# Revit family: super-g_super-g___l_1150mm_hl_dir_indirekt_led__27_6w_4260lm_3000k_cri_80_dali__430-1542_0726
name_source: partatom
category: Leuchten
revit_build: Autodesk Revit 2016 (Build: 20190508_0715(x64)
units: mm (PartAtom-declared; Revit-internal decimal feet)

## family parameters
Basisbauteil = Fläche
Beim Laden mit Abzugskörper schneiden = Nein
Bemaßung runder Anschluss = Durchmesser verwenden
Gemeinsam genutzt = Nein
Lichtquelle = Nein
Raumberechnungspunkt = Nein
Teiletyp = Normal

## types (1)
- 430-1542- (6 x LED, 710 lm, 5.1 W, 3000K)
    Approval mark = CE
    Beschreibung = The insert consists of aluminum-extruded profile. Charming SOFT-EDGE design ensure unparalleled styling. The ballast is integrated and allows for an operation with 220-240V (50/60Hz). SUPER-G (# 430-1542) is dimmable via BUS.
    CIE Flux Codes = 48 80 96 61 70
    Color Rendering = 1B/80…89
    Color Temperature = 3000K
    Height = 120 mm
    Hersteller = Prolicht
    Lamp Light Flux = 710 lm
    Lamp Power = 5.1 W
    Lamp count = 6
    Lampe = 6 x LED
    Length = 1150 mm
    Luminous efficacy = 97 lm/W
    ModVariant = Nein
    Modell = 430-1542
    Mounting Place = Ceiling
    Mounting Type = Pendant
    Number of Poles = 1
    OnlyDefault = Ja
    Power Factor = 1
    Product Name = SUPER-G__SUPER-G   L=1150mm HL dir/indirekt LED: 27,6W 4260lm 3000K CRI:80 DALI
    Product group = Suspended profile systems
    ProductGroupID = 944
    Protection Class = Protection class I
    Protection Degree = IP 20
    RLX_Detail_Level = 1
    RlxData = <blob elided: 17589 chars, md5=be66f0f7>
    Scheinlast = 31 VA
    Socket = socket
    Standby Power = 0 W
    System Light Flux = 2974 lm
    System Power = 31 W
    Typenbild = 430-1542.jpg
    URL = http://relux.com
    VarID = 430-1542-
    Voltage = 0 V
    Vorgabe-Ansicht = 1800 mm
    Weight = 0.00 kg
    Width = 150 mm

## geometry (parser evidence)
native form markers: Blend x4, Sweep x10
no freeform markers — native parametric forms only
